# Revit family: Basin-Wall_Hung-Grohe-Eurocube-3965_Series
name_source: partatom
category: Plumbing Fixtures
revit_build: Autodesk Revit 2014 (Build: 20130308_1515(x64)
units: mm (PartAtom-declared; Revit-internal decimal feet)

## types (2) — shared parameters
39657000 - Eurocube Sink Shroud = No
ADA Compliant = Yes
Assembly Code = D2010310
Basin Shape = Rectangular
CW Connection = Yes
CWFU = 1.5
Cold Water Connection Radius = 3/16"
Countertop Installation = No
Default Elevation = 34"
Description = Eurocube Wall Mount/Above Counter Lavatory
Finish = Fine Fire Clay-Grohe-000-Alpine White
HW Connection = Yes
HWFU = 1.5
Height = 5 7/16"
Hot Water Connection Radius = 3/16"
Installation Type = Wall-Hung
Length = 19 1/16"
Manufacturer = Grohe
Material = Fine Fire Clay-Grohe-000-Alpine White
Model = 39655000
Price = Prices may vary. Please consult Manufacturer Representative for most up-to-date price list.
URL = https://www.grohe.us
Vent Connection = No
WFU = 2
Waste Connection = Yes
Waste Connection Radius = 5/8"
Width = 24 3/16"

## per-type parameters (varying)
| type | 8" Centerset | Hole Height |
| 39655000 | Yes | 5" |
| 39656000 | No | 1" |

## geometry (parser evidence)
native form markers: Blend x10, Sweep x1
no freeform markers — native parametric forms only
